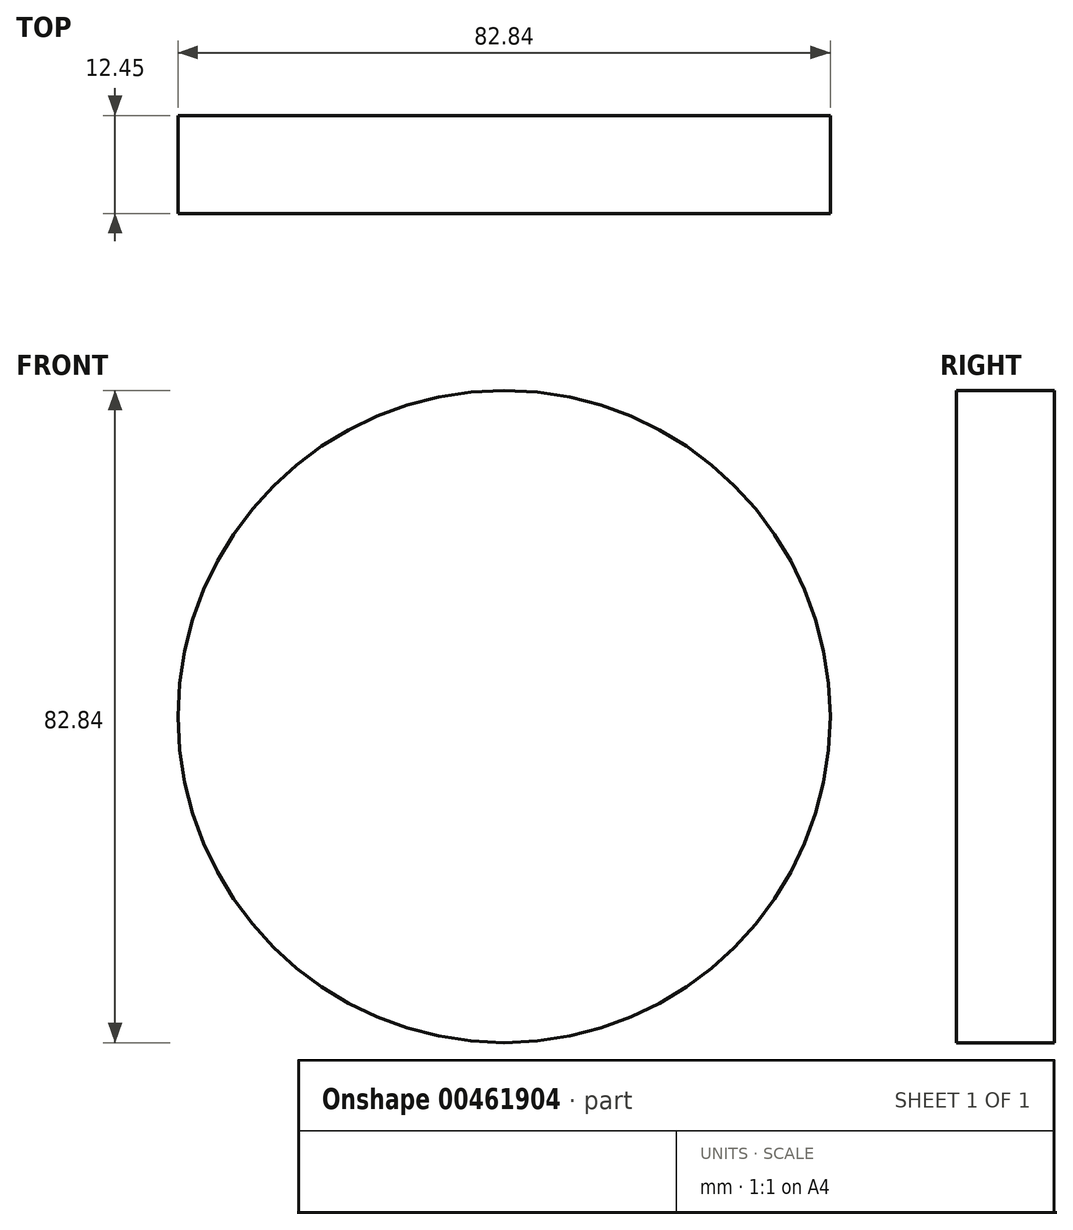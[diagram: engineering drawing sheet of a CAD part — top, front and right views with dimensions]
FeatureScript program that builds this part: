
annotation { "Feature Type Name" : "Feature", "Feature Type Description" : "" }
export const myFeature = defineFeature(function(context is Context, id is Id, definition is map)
    precondition{}
    {
        {
            var Q0;
            Q0=qCreatedBy(makeId("Front.planeOp"),FACE);
            var sketch = newSketch(context, id + "F0", { "sketchPlane" : qUnion([Q0])});
            skCircle(sketch, "E0", {"center": v(0, 0) * mm, "radius": 41.42 * mm});
            skSolve(sketch);
        }
        {
            var Q0;
            Q0 = qSketchRegion(id + "F0", true);
            extrude(context, id + "F1", {"entities" : qUnion([Q0]), "depth" : 12.45 * mm});
        }
    });
